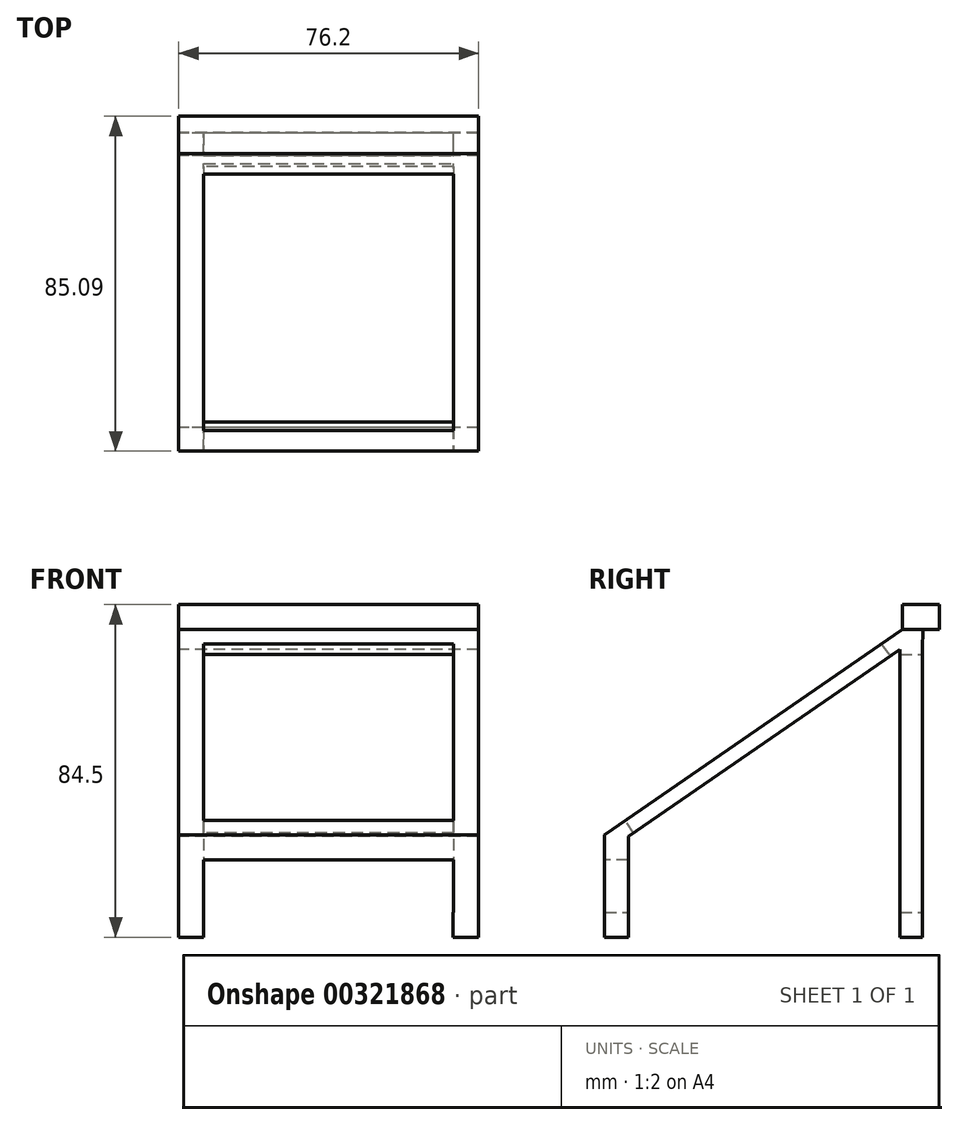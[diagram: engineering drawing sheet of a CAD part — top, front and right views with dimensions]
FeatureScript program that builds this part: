
annotation { "Feature Type Name" : "Feature", "Feature Type Description" : "" }
export const myFeature = defineFeature(function(context is Context, id is Id, definition is map)
    precondition{}
    {
        {
            var Q0;
            Q0=qCreatedBy(makeId("Right.planeOp"),FACE);
            var sketch = newSketch(context, id + "F0", { "sketchPlane" : qUnion([Q0])});
            skLineSegment(sketch, "E0.bottom", {"start": v(-63.23, 0) * mm, "end": v(-57.18, 0) * mm});
            skLineSegment(sketch, "E0.top", {"start": v(-63.23, 21.44) * mm, "end": v(-57.18, 21.44) * mm});
            skLineSegment(sketch, "E0.left", {"start": v(-63.23, 0) * mm, "end": v(-63.23, 21.44) * mm});
            skLineSegment(sketch, "E0.right", {"start": v(-57.18, 0) * mm, "end": v(-57.18, 21.44) * mm});
            skLineSegment(sketch, "E1.bottom", {"start": v(11.82, 0) * mm, "end": v(17.53, 0) * mm});
            skLineSegment(sketch, "E1.top", {"start": v(11.82, 73.13) * mm, "end": v(17.53, 73.13) * mm});
            skLineSegment(sketch, "E1.left", {"start": v(11.82, 0) * mm, "end": v(11.82, 73.13) * mm});
            skLineSegment(sketch, "E1.right", {"start": v(17.53, 0) * mm, "end": v(17.53, 73.13) * mm});
            skLineSegment(sketch, "E2", {"start": v(-63.23, 21.44) * mm, "end": v(11.82, 73.13) * mm});
            skLineSegment(sketch, "E3", {"start": v(-57.18, 21.44) * mm, "end": v(-57.18, 25.6) * mm});
            skLineSegment(sketch, "E4", {"start": v(-63.23, 21.44) * mm, "end": v(-63.23, 26.03) * mm});
            skLineSegment(sketch, "E5", {"start": v(-63.23, 26.03) * mm, "end": v(12.43, 78.15) * mm});
            skLineSegment(sketch, "E6", {"start": v(12.43, 78.15) * mm, "end": v(17.53, 73.13) * mm});
            skLineSegment(sketch, "E7", {"start": v(11.82, 73.13) * mm, "end": v(12.43, 78.15) * mm});
            skLineSegment(sketch, "E8", {"start": v(12.43, 78.15) * mm, "end": v(17.66, 78.15) * mm});
            skLineSegment(sketch, "E9", {"start": v(17.66, 78.15) * mm, "end": v(17.53, 73.13) * mm});
            skSolve(sketch);
        }
        {
            var Q0;
            Q0 = qSketchRegion(id + "F0", true);
            extrude(context, id + "F1", {"entities" : qUnion([Q0]), "endBound" : BoundingType.SYMMETRIC, "depth" : 76.2 * mm});
        }
        {
            var Q0;
            Q0=makeQuery(id+"F1.opExtrude","SWEPT_FACE",FACE,{"disambiguationData":[OSD([sQuery(id+"F0.wireOp",EDGE,"E5")])]});
            var sketch = newSketch(context, id + "F2", { "sketchPlane" : qUnion([Q0])});
            skLineSegment(sketch, "E10.0", {"start": v(-31.75, -30.95) * mm, "end": v(-31.75, 48.22) * mm});
            skLineSegment(sketch, "E10.1", {"start": v(31.75, -30.95) * mm, "end": v(-31.75, -30.95) * mm});
            skLineSegment(sketch, "E10.2", {"start": v(31.75, -30.95) * mm, "end": v(31.75, 48.22) * mm});
            skLineSegment(sketch, "E10.3", {"start": v(31.75, 48.22) * mm, "end": v(-31.75, 48.22) * mm});
            skSolve(sketch);
        }
        {
            var Q0;
            Q0=makeQuery(id+"F2.imprint","IMPRINT",FACE,{"disambiguationData":[TD([[makeQuery(id+"F2.imprint","IMPRINT",EDGE,{"derivedFrom":sQuery(id+"F2.wireOp",EDGE,"E10.0")}),-1.0]])]});
            extrude(context, id + "F3", {"entities" : qUnion([Q0]), "operationType" : NewBodyOperationType.REMOVE, "oppositeDirection" : true, "depth" : 6.35 * mm});
        }
        {
            var Q0;
            Q0=makeQuery(id+"F1.opExtrude","SWEPT_FACE",FACE,{"disambiguationData":[OSD([sQuery(id+"F0.wireOp",EDGE,"E1.right")])]});
            var sketch = newSketch(context, id + "F4", { "sketchPlane" : qUnion([Q0])});
            skLineSegment(sketch, "E11.0", {"start": v(-31.75, 6.35) * mm, "end": v(31.75, 6.35) * mm});
            skLineSegment(sketch, "E11.1", {"start": v(-31.75, 71.8) * mm, "end": v(-31.75, 69.92) * mm});
            skLineSegment(sketch, "E11.2", {"start": v(-31.75, 71.8) * mm, "end": v(31.75, 71.8) * mm});
            skLineSegment(sketch, "E11.3", {"start": v(-31.75, 6.35) * mm, "end": v(-31.75, 69.92) * mm});
            skLineSegment(sketch, "E11.4", {"start": v(31.75, 71.8) * mm, "end": v(31.75, 69.92) * mm});
            skLineSegment(sketch, "E11.5", {"start": v(31.75, 6.35) * mm, "end": v(31.75, 69.92) * mm});
            skSolve(sketch);
        }
        {
            var Q0;
            Q0=makeQuery(id+"F4.imprint","IMPRINT",FACE,{"disambiguationData":[TD([[makeQuery(id+"F4.imprint","IMPRINT",EDGE,{"derivedFrom":sQuery(id+"F4.wireOp",EDGE,"E11.0")}),1.0]])]});
            extrude(context, id + "F5", {"entities" : qUnion([Q0]), "operationType" : NewBodyOperationType.REMOVE, "oppositeDirection" : true, "depth" : 5.08 * mm});
        }
        {
            var Q0;
            Q0=makeQuery(id+"F5.boolean.opBoolean","COPY",FACE,{"derivedFrom":makeQuery(id+"F5.opExtrude","CAP_FACE",FACE,{"disambiguationData":[OSD([sQuery(id+"F0.wireOp",EDGE,"E1.top"),sQuery(id+"F0.wireOp",EDGE,"E1.right"),sQuery(id+"F0.wireOp",EDGE,"E6"),sQuery(id+"F4.wireOp",EDGE,"E11.0"),sQuery(id+"F4.wireOp",EDGE,"E11.3"),sQuery(id+"F4.wireOp",EDGE,"E11.5")])],"isStart":false})});
            extrude(context, id + "F6", {"entities" : qUnion([Q0]), "operationType" : NewBodyOperationType.REMOVE, "oppositeDirection" : true, "depth" : 12.7 * mm});
        }
        {
            var Q0;
            Q0=makeQuery(id+"F1.opExtrude","SWEPT_FACE",FACE,{"disambiguationData":[OSD([sQuery(id+"F0.wireOp",EDGE,"E0.left"),sQuery(id+"F0.wireOp",EDGE,"E4")])]});
            var sketch = newSketch(context, id + "F7", { "sketchPlane" : qUnion([Q0])});
            skLineSegment(sketch, "E12.0", {"start": v(31.75, 19.68) * mm, "end": v(-31.75, 19.68) * mm});
            skLineSegment(sketch, "E12.1", {"start": v(31.75, 6.35) * mm, "end": v(31.75, 19.68) * mm});
            skLineSegment(sketch, "E12.2", {"start": v(31.75, 6.35) * mm, "end": v(-31.75, 6.35) * mm});
            skLineSegment(sketch, "E12.3", {"start": v(-31.75, 6.35) * mm, "end": v(-31.75, 19.68) * mm});
            skSolve(sketch);
        }
        {
            var Q0;
            Q0=makeQuery(id+"F7.imprint","IMPRINT",FACE,{"disambiguationData":[TD([[makeQuery(id+"F7.imprint","IMPRINT",EDGE,{"derivedFrom":sQuery(id+"F7.wireOp",EDGE,"E12.0")}),1.0]])]});
            extrude(context, id + "F8", {"entities" : qUnion([Q0]), "operationType" : NewBodyOperationType.REMOVE, "oppositeDirection" : true, "depth" : 6.35 * mm});
        }
        {
            var Q0;
            Q0=makeQuery(id+"F7.imprint","IMPRINT",FACE,{"disambiguationData":[TD([[makeQuery(id+"F7.imprint","IMPRINT",EDGE,{"derivedFrom":sQuery(id+"F7.wireOp",EDGE,"E12.0")}),-1.0]])]});
            var sketch = newSketch(context, id + "F9", { "sketchPlane" : qUnion([Q0])});
            skLineSegment(sketch, "E13.bottom", {"start": v(-31.76, 0) * mm, "end": v(31.6, 0) * mm});
            skLineSegment(sketch, "E13.top", {"start": v(-31.76, 6.35) * mm, "end": v(31.6, 6.35) * mm});
            skLineSegment(sketch, "E13.left", {"start": v(-31.76, 0) * mm, "end": v(-31.76, 6.35) * mm});
            skLineSegment(sketch, "E13.right", {"start": v(31.6, 0) * mm, "end": v(31.6, 6.35) * mm});
            skSolve(sketch);
        }
        {
            var Q0;
            Q0=makeQuery(id+"F9.imprint","IMPRINT",FACE,{"disambiguationData":[TD([[makeQuery(id+"F9.imprint","IMPRINT",EDGE,{"derivedFrom":sQuery(id+"F9.wireOp",EDGE,"E13.bottom")}),-1.0]])]});
            extrude(context, id + "F10", {"entities" : qUnion([Q0]), "operationType" : NewBodyOperationType.REMOVE, "oppositeDirection" : true, "depth" : 508 * mm});
        }
        {
            var Q0;
            Q0=makeQuery(id+"F1.opExtrude","SWEPT_FACE",FACE,{"disambiguationData":[OSD([sQuery(id+"F0.wireOp",EDGE,"E8")])]});
            var sketch = newSketch(context, id + "F11", { "sketchPlane" : qUnion([Q0])});
            skLineSegment(sketch, "E14.bottom", {"start": v(-38.1, 12.43) * mm, "end": v(38.08, 12.43) * mm});
            skLineSegment(sketch, "E14.top", {"start": v(-38.1, 21.86) * mm, "end": v(38.08, 21.86) * mm});
            skLineSegment(sketch, "E14.left", {"start": v(-38.1, 12.43) * mm, "end": v(-38.1, 21.86) * mm});
            skLineSegment(sketch, "E14.right", {"start": v(38.08, 12.43) * mm, "end": v(38.08, 21.86) * mm});
            skSolve(sketch);
        }
        {
            var Q0;
            Q0 = qSketchRegion(id + "F11", true);
            extrude(context, id + "F12", {"entities" : qUnion([Q0]), "operationType" : NewBodyOperationType.ADD, "depth" : 6.35 * mm});
        }
        {
            var Q0;
            Q0=makeQuery(id+"F12.opExtrude","CAP_FACE",FACE,{"disambiguationData":[OSD([sQuery(id+"F11.wireOp",EDGE,"E14.bottom"),sQuery(id+"F11.wireOp",EDGE,"E14.top"),sQuery(id+"F11.wireOp",EDGE,"E14.left"),sQuery(id+"F11.wireOp",EDGE,"E14.right")])],"isStart":false});
            var sketch = newSketch(context, id + "F13", { "sketchPlane" : qUnion([Q0])});
            skCircle(sketch, "E15", {"center": v(0, 17.87) * mm, "radius": 0.9 * mm});
            skSolve(sketch);
        }
        {
            var Q0;
            Q0=makeQuery(id+"F13.imprint","IMPRINT",FACE,{"disambiguationData":[TD([[makeQuery(id+"F13.imprint","IMPRINT",EDGE,{"derivedFrom":sQuery(id+"F13.wireOp",EDGE,"E15")}),1.0]])]});
            extrude(context, id + "F14", {"entities" : qUnion([Q0]), "operationType" : NewBodyOperationType.ADD, "oppositeDirection" : true, "depth" : 0.5 * mm});
        }
    });
